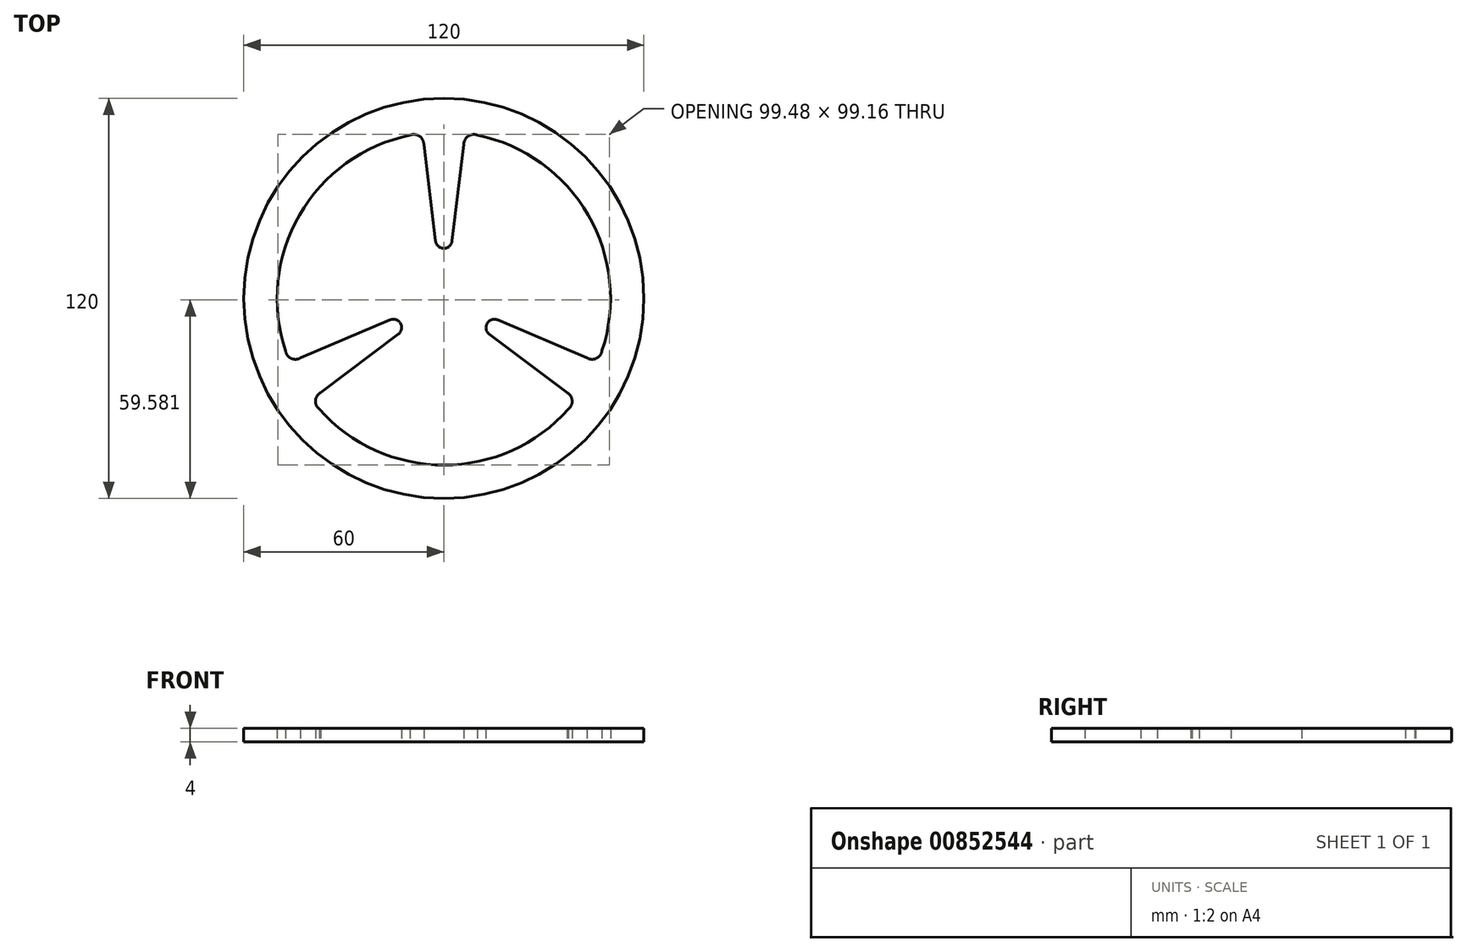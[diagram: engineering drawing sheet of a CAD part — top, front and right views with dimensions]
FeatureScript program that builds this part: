
annotation { "Feature Type Name" : "Feature", "Feature Type Description" : "" }
export const myFeature = defineFeature(function(context is Context, id is Id, definition is map)
    precondition{}
    {
        {
            var Q0;
            Q0=qCreatedBy(makeId("Top.planeOp"),FACE);
            var sketch = newSketch(context, id + "F0", { "sketchPlane" : qUnion([Q0])});
            skCircle(sketch, "E0", {"center": v(0, 0) * mm, "radius": 60 * mm});
            skPoint(sketch, "E1", {"position": v(6, 46.18) * mm});
            skPoint(sketch, "E2", {"position": v(10.1, 48.97) * mm});
            skArc(sketch, "E3", {"start": v(10.1, 48.97) * mm, "mid": v(7.32, 48.66) * mm, "end": v(6, 46.18) * mm});
            skArc(sketch, "E4.MirrorCS", {"start": v(-10.1, 48.97) * mm, "mid": v(-7.32, 48.66) * mm, "end": v(-6, 46.18) * mm});
            skArc(sketch, "E5.trimOffspring", {"start": v(-10.1, 48.97) * mm, "mid": v(-43.58, 24.52) * mm, "end": v(-47.1, -16.78) * mm});
            skArc(sketch, "E6", {"start": v(-2.48, 17.2) * mm, "mid": v(0, 15) * mm, "end": v(2.48, 17.2) * mm});
            skLineSegment(sketch, "E7", {"start": v(6, 46.18) * mm, "end": v(2.48, 17.2) * mm});
            skLineSegment(sketch, "E8", {"start": v(-6, 46.18) * mm, "end": v(-2.48, 17.2) * mm});
            skArc(sketch, "E9.1.0", {"start": v(-37.35, -33.24) * mm, "mid": v(-38.48, -30.67) * mm, "end": v(-37, -28.29) * mm});
            skLineSegment(sketch, "E9.1.1", {"start": v(-37, -28.29) * mm, "end": v(-13.65, -10.75) * mm});
            skArc(sketch, "E9.1.2", {"start": v(-13.65, -10.75) * mm, "mid": v(-13, -7.5) * mm, "end": v(-16.14, -6.45) * mm});
            skLineSegment(sketch, "E9.1.3", {"start": v(-43, -17.9) * mm, "end": v(-16.14, -6.45) * mm});
            skArc(sketch, "E9.1.4", {"start": v(-47.46, -15.73) * mm, "mid": v(-45.8, -18) * mm, "end": v(-43, -17.9) * mm});
            skArc(sketch, "E9.2.0", {"start": v(47.46, -15.73) * mm, "mid": v(45.8, -18) * mm, "end": v(43, -17.9) * mm});
            skLineSegment(sketch, "E9.2.1", {"start": v(43, -17.9) * mm, "end": v(16.14, -6.45) * mm});
            skArc(sketch, "E9.2.2", {"start": v(16.14, -6.45) * mm, "mid": v(13, -7.5) * mm, "end": v(13.65, -10.75) * mm});
            skLineSegment(sketch, "E9.2.3", {"start": v(37, -28.29) * mm, "end": v(13.65, -10.75) * mm});
            skArc(sketch, "E9.2.4", {"start": v(37.35, -33.24) * mm, "mid": v(38.48, -30.67) * mm, "end": v(37, -28.29) * mm});
            skArc(sketch, "E10.trimOffspring", {"start": v(-38.08, -32.4) * mm, "mid": v(0, -50) * mm, "end": v(38.08, -32.4) * mm});
            skArc(sketch, "E11.trimOffspring", {"start": v(47.1, -16.78) * mm, "mid": v(43.58, 24.52) * mm, "end": v(10.1, 48.97) * mm});
            skSolve(sketch);
        }
        {
            var Q0;
            {var subQ18=sQuery(id+"F0.wireOp",EDGE,"E3");Q0=makeQuery(id+"F0.imprint","IMPRINT",FACE,{"disambiguationData":[TD([[makeQuery(id+"F0.imprint","IMPRINT",EDGE,{"derivedFrom":subQ18}),-1.0]])]});}
            extrude(context, id + "F1", {"entities" : qUnion([Q0]), "depth" : 4 * mm, "offsetDistance" : 25 * mm});
        }
    });
